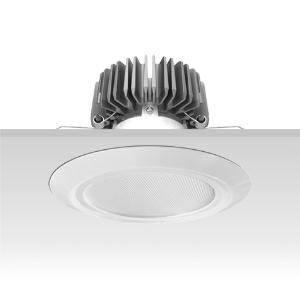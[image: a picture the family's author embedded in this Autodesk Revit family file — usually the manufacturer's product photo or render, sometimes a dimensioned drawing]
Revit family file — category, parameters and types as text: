
# Revit family: 3f_filippi_-_3f_reno_bianco_ampio_3f_filippi_-_30679_a01048_-_3f_reno_200_wh_3000-840_dali_wide___smp_wh_e104
name_source: partatom
category: Lighting Fixtures
units: mm (PartAtom-declared; Revit-internal decimal feet)

## family parameters
Cut with Voids When Loaded = No
Host = Face
Light Source = No
Part Type = Normal
Room Calculation Point = No
Round Connector Dimension = Use Diameter
Shared = No

## types (1)
- 3F Filippi - 3F Reno Bianco Ampio (1 x LED, 2312 lm, 28 W, 4000 K)
    Apparent Load = 28 VA
    Approval mark = CE
    CIE Flux Codes = 74 92 98 100 100
    Color Rendering = 80
    Color Temperature = 4000 K
    Control Gear = Electronic transformer
    Default Elevation = 1800 mm
    Description = ILLUMINOTECHNICAL
Luminous efficiency 100% (DLOR 100%, ULOR 0%).
Initial luminous flux of the luminaire 2312 lm.
Direct symmetric wide distribution.
Installation Interdistance Transv.D = 1.06 x hu - Long.D = 1.04 x hu.
Tabular UGR (CIE 117 - 4H-8H; S=0.25H; 70/50/20): RUG 22.5 - 22.3.
Beam angle: 70° - 69°.
Luminous efficacy 83 lm/W.
Lifetime (L90/B10): 30000 h. (tq+25°C)
Lifetime (L85/B10): 50000 h. (tq+25°C)
Lifetime (L70/B10): 80000 h. (tq+25°C)
Sudden decreased luminous flux after 50000 hours: 0% (C0).
Photobiological safety in compliance with IEC/TR 62778: RG0 risk exempt, (IEC 62471).
In compliance with IEC/EN 62722-2-1 - IEC/EN 62717 standards.

SOURCE
Compact LED module 3000/840.
Energy efficiency class (UE 2019/2020 - UE 2019/2015): E.
CIE 13.3 Colour rendering index: CRI >80 (R9 <50%).
IES TM-30 Fidelity Index: Rf = 84 Rg = 95.
CCT nominal colour temperature 4000 K.
Colour initial tolerance (MacAdam): SDCM 3.
Zhaga Book 3 compliant.

MECHANICAL
Passive heat dissipator in die-casting aluminium, oversized, for optimum thermal management of the LED module.
Parabolic element with graduated/concentric rings in white polycarbonate.
Transparent external lens with glossy and satin differentiated surfaces, with a cooling and anti-insect system in methacrylate (PMMA).
Fastening spring clips in stainless steel.
Dimensions: diameter 226 mm, height 146 mm. Weight 1.695 kg.
IP44 protection degree for exposed part, IP20 for recessed part.
Mechanical strength to impacts IK05 (0.7 joule).
Glow-wire test resistance 650°C.

ELECTRICAL
Wiring on a separate unit.
Halogen Free DALI-2 DATI (Parts 251, 252, 253), PUSH-DIM, electronic wiring 230V-50/60Hz, power factor 0.97 at full load, THD <25%, constant output current, SELV, class II, 1 driver, 1 DALI addresse.
Power of the luminaire 28 W.
ENEC - CE.
SAFE FLICKER: PstLM=<1 and SVM=<0.4 (IEC TR 61547-1 and IEC TR 63158), to ensure a more comfortable and safe light.
Luminaire compliant with EN 60598-2-22 for power supply from a centralised emergency system CPSS (Central Power Supply System), not incorporated in the luminaire - high risk areas excluded. The default power and flux are 100% in AC and 100% in DC.
Ambient temperature from 0°C to +25°C.
Temperature class T6 max 85°C.
Relative humidity UR: <85%.

INSTALLATION
Pull-up recessed fitting.
False ceiling carving: 200 mm.
All accessories dedicated to this product are available on the Catalog and on our website www.3F-Filippi.com.

ACCESSORIES
A01048 - Anti-glare microprismatic SMP diffuser in methacrylate (PMMA), locked and in line with the trim, in white polycarbonate.

APPLICATIONS
Suitable product for food production plants (HACCP), IFS (Food Version 6), BRC (GSFS Food Version 7).
Environments: architectural, commercial, exhibition areas, transit areas, corridors, shops, display windows, service areas.
In false ceilings with narrow voids.

LIGHT MANAGEMENT
Recommended minimum setting: 10%.
The luminaire, equipped with (DALI-2 DATI) driver, can be controlled manually with 3F Easy Dim technology or automatically/manually with wired or wireless DALI/D2D control systems.
The D2D driver guarantees interoperability with other devices with the same certification by making the following information available:
Device Data (Part 251), Energy Report (Part 252), Diagnosis & Maintenance (Part 253).
In electrical systems without a regulation system (manual or automatic) and DALI bus, a suitable jumper must be made on the DA-DA terminals of the appliance.

WARNING
Luminaire designed for disposal/recycling at end-of-life.
Replaceable (LED only) light source by a professional. Replaceable control gear by a professional.
    Height = 0 mm  [stored 0 ft]
    Lamp = 1 x LED
    Lamp Light Flux = 2312 lm
    Lamp Power = 28 W
    Lamp count = 1
    Length = 226 mm
    Lifetime = 50000 h
    Luminous efficacy = 83 lm/W
    Manufacturer = 3F Filippi
    ModVariant = No
    Model = 3F Filippi - 30679+A01048 - 3F Reno 200 WH 3000-840 DALI WIDE + SMP WH
    Mounting Place = Ceiling
    Mounting Type = Recessed
    Number of Poles = 1
    OnlyDefault = Yes
    Power Factor = 1
    Product Name = 3F Filippi - 3F Reno Bianco Ampio
    Product group = recessed luminaire
    ProductGroupID = 4
    Protection Class = Protection class II
    Protection Degree = IP 20
    RLX_Detail_Level = 1
    RLX_Emergency_Light_Flux = 0 lm
    RLX_Emergency_Type = 0
    RLX_Emergency_Type_DB = No
    RlxData = <blob elided: 97577 chars, md5=5475f04f>
    Socket = socket
    Standby Power = 0 W
    System Light Flux = 2312 lm
    System Power = 28 W
    Type Comments = Product without accessories
    Type Image = 3ffilippi_3f_reno_200_wh_vs_smp.jpg
    URL = http://relux.com
    VarID = ---
    Voltage = 0 V
    Weight = 0.00 kg
    Width = 0 mm  [stored 0 ft]

note: [stored X ft] marks values corroborated as IEEE doubles in the binary element streams (Revit-internal decimal feet)

## geometry (parser evidence)
native form markers: Blend x4, Sweep x9
no freeform markers — native parametric forms only
